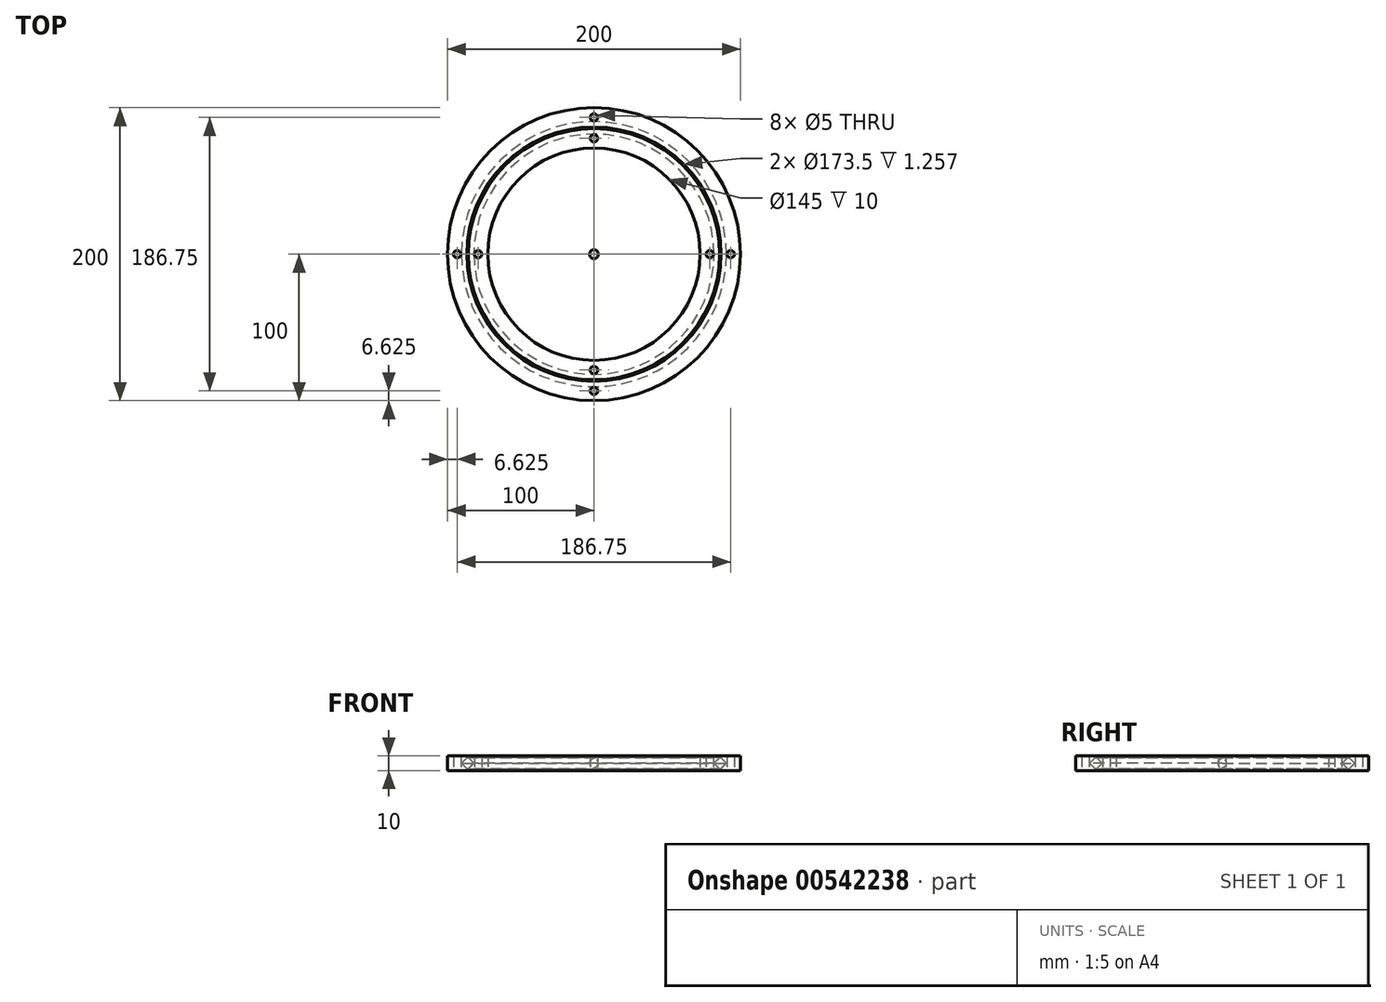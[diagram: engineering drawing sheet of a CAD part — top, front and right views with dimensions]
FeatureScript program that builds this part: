
annotation { "Feature Type Name" : "Feature", "Feature Type Description" : "" }
export const myFeature = defineFeature(function(context is Context, id is Id, definition is map)
    precondition{}
    {
        {
            assignVariable(context, id + "F0", {"name" : "h", "anyValue" : 10});
        }
        {
            var Q0;
            Q0=qCreatedBy(makeId("Top.planeOp"),FACE);
            var sketch = newSketch(context, id + "F1", { "sketchPlane" : qUnion([Q0])});
            skCircle(sketch, "E0", {"center": v(0, 0) * mm, "radius": 100 * mm});
            skCircle(sketch, "E1", {"center": v(0, 0) * mm, "radius": 86.75 * mm});
            skLineSegment(sketch, "E2", {"start": v(0, 108.79) * mm, "end": v(0, -107.46) * mm, "construction": true});
            skLineSegment(sketch, "E3", {"start": v(-112.1, 0) * mm, "end": v(109.19, 0) * mm, "construction": true});
            skCircle(sketch, "E4", {"center": v(0, 0) * mm, "radius": 93.38 * mm, "construction": true});
            skCircle(sketch, "E5", {"center": v(0, 93.38) * mm, "radius": 2.5 * mm});
            skCircle(sketch, "E6.1.0", {"center": v(-93.38, 0) * mm, "radius": 2.5 * mm});
            skCircle(sketch, "E6.2.0", {"center": v(0, -93.38) * mm, "radius": 2.5 * mm});
            skCircle(sketch, "E7.1.3.0", {"center": v(93.38, 0) * mm, "radius": 2.5 * mm});
            skSolve(sketch);
        }
        {
            var Q0;
            Q0 = qSketchRegion(id + "F1", true);
            extrude(context, id + "F2", {"entities" : qUnion([Q0]), "endBound" : BoundingType.SYMMETRIC, "depth" : (getVariable(context, 'h')) * mm, "offsetDistance" : 25 * mm});
        }
        {
            var Q0;
            Q0=qCreatedBy(makeId("Top.planeOp"),FACE);
            var sketch = newSketch(context, id + "F3", { "sketchPlane" : qUnion([Q0])});
            skCircle(sketch, "E8", {"center": v(0, 0) * mm, "radius": 85.75 * mm});
            skCircle(sketch, "E9", {"center": v(0, 0) * mm, "radius": 72.5 * mm});
            skCircle(sketch, "E10", {"center": v(0, 0) * mm, "radius": 79.12 * mm, "construction": true});
            skCircle(sketch, "E11", {"center": v(0, 79.12) * mm, "radius": 2.5 * mm});
            skCircle(sketch, "E12.1.0", {"center": v(-79.12, 0) * mm, "radius": 2.5 * mm});
            skCircle(sketch, "E12.2.0", {"center": v(0, -79.12) * mm, "radius": 2.5 * mm});
            skCircle(sketch, "E13.1.3.0", {"center": v(79.12, 0) * mm, "radius": 2.5 * mm});
            skSolve(sketch);
        }
        {
            var Q0;
            Q0 = qSketchRegion(id + "F3", true);
            extrude(context, id + "F4", {"entities" : qUnion([Q0]), "endBound" : BoundingType.SYMMETRIC, "depth" : (getVariable(context, 'h')) * mm, "offsetDistance" : 25 * mm});
        }
        {
            var Q0;
            Q0=qCreatedBy(makeId("Front.planeOp"),FACE);
            var sketch = newSketch(context, id + "F5", { "sketchPlane" : qUnion([Q0])});
            skCircle(sketch, "E14", {"center": v(86.25, 0) * mm, "radius": 3 * mm, "construction": true});
            skLineSegment(sketch, "E15", {"start": v(86.25, 4.24) * mm, "end": v(82, 0) * mm});
            skLineSegment(sketch, "E16", {"start": v(82, 0) * mm, "end": v(86.25, -4.24) * mm});
            skLineSegment(sketch, "E17", {"start": v(86.25, 4.24) * mm, "end": v(90.5, 0) * mm});
            skLineSegment(sketch, "E18", {"start": v(90.5, 0) * mm, "end": v(86.25, -4.24) * mm});
            skSolve(sketch);
        }
        {
            var Q0;
            Q0 = qSketchRegion(id + "F5", true);
            var Q1;
            Q1=makeQuery(id+"F4.opExtrude","SWEPT_FACE",FACE,{"disambiguationData":[OSD([sQuery(id+"F3.wireOp",EDGE,"E9")])]});
            revolve(context, id + "F6", {"entities" : qUnion([Q0]), "axis" : qUnion([Q1]), "revolveType" : RevolveType.FULL});
        }
        {
            var Q0;
            Q0=makeQuery(id+"F6.opRevolve","SWEPT_BODY",BODY,{"disambiguationData":[OSD([sQuery(id+"F5.wireOp",EDGE,"E15"),sQuery(id+"F5.wireOp",EDGE,"E16"),sQuery(id+"F5.wireOp",EDGE,"E17"),sQuery(id+"F5.wireOp",EDGE,"E18")])]});
            var Q1;
            Q1=makeQuery(id+"F2.opExtrude","SWEPT_BODY",BODY,{"disambiguationData":[OSD([sQuery(id+"F1.wireOp",EDGE,"E0"),sQuery(id+"F1.wireOp",EDGE,"E1"),sQuery(id+"F1.wireOp",EDGE,"E5"),sQuery(id+"F1.wireOp",EDGE,"E6.1.0"),sQuery(id+"F1.wireOp",EDGE,"E6.2.0"),sQuery(id+"F1.wireOp",EDGE,"E7.1.3.0")])]});
            var Q2;
            Q2=makeQuery(id+"F4.opExtrude","SWEPT_BODY",BODY,{"disambiguationData":[OSD([sQuery(id+"F3.wireOp",EDGE,"E8"),sQuery(id+"F3.wireOp",EDGE,"E9"),sQuery(id+"F3.wireOp",EDGE,"E11"),sQuery(id+"F3.wireOp",EDGE,"E12.1.0"),sQuery(id+"F3.wireOp",EDGE,"E12.2.0"),sQuery(id+"F3.wireOp",EDGE,"E13.1.3.0")])]});
            booleanBodies(context, id + "F7", {"operationType" : BooleanOperationType.SUBTRACTION, "tools" : qUnion([Q0]), "targets" : qUnion([Q1, Q2])});
        }
        {
            var Q0;
            Q0=qCreatedBy(makeId("Front.planeOp"),FACE);
            var sketch = newSketch(context, id + "F8", { "sketchPlane" : qUnion([Q0])});
            skArc(sketch, "E19", {"start": v(0, -3) * mm, "mid": v(3, 0) * mm, "end": v(0, 3) * mm});
            skLineSegment(sketch, "E20", {"start": v(0, 3) * mm, "end": v(0, -3) * mm});
            skSolve(sketch);
        }
        {
            var Q0;
            Q0 = qSketchRegion(id + "F8", true);
            var Q1;
            Q1=sQuery(id+"F8.wireOp",EDGE,"E20");
            revolve(context, id + "F9", {"entities" : qUnion([Q0]), "axis" : qUnion([Q1]), "revolveType" : RevolveType.FULL});
        }
    });
